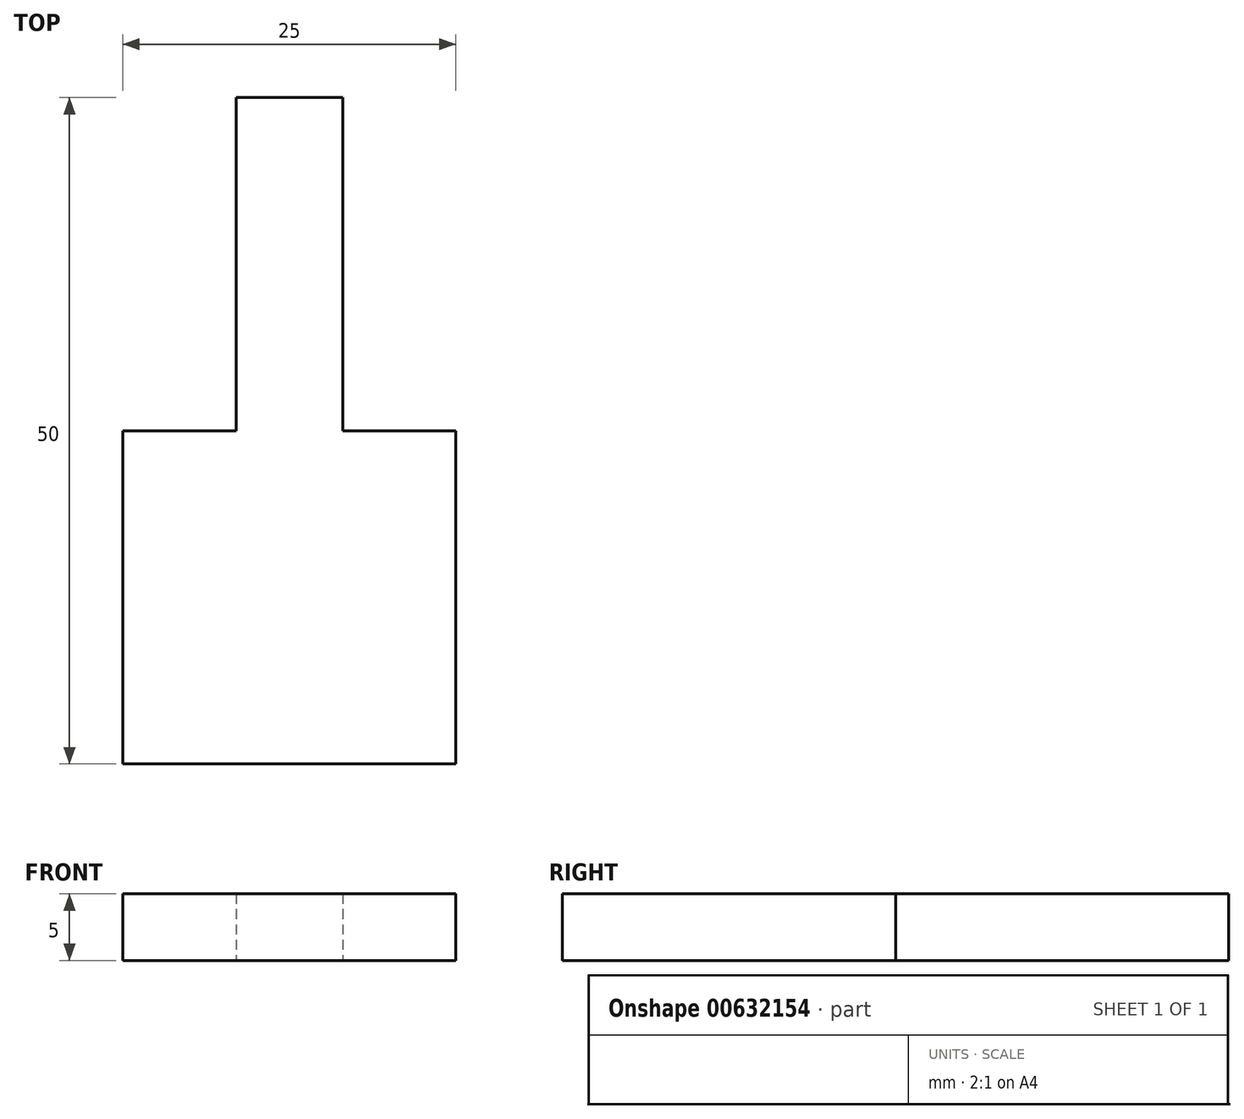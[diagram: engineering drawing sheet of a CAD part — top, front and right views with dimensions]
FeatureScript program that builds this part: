
annotation { "Feature Type Name" : "Feature", "Feature Type Description" : "" }
export const myFeature = defineFeature(function(context is Context, id is Id, definition is map)
    precondition{}
    {
        {
            var Q0;
            Q0=qCreatedBy(makeId("Top.planeOp"),FACE);
            var sketch = newSketch(context, id + "F0", { "sketchPlane" : qUnion([Q0])});
            skLineSegment(sketch, "E0.bottom", {"start": v(4, -12.5) * mm, "end": v(-4, -12.5) * mm});
            skLineSegment(sketch, "E0.top", {"start": v(4, 12.5) * mm, "end": v(-4, 12.5) * mm});
            skLineSegment(sketch, "E0.left", {"start": v(4, -12.5) * mm, "end": v(4, 12.5) * mm});
            skLineSegment(sketch, "E0.right", {"start": v(-4, -12.5) * mm, "end": v(-4, 12.5) * mm});
            skPoint(sketch, "E0.middle", {"position": v(0, 0) * mm});
            skLineSegment(sketch, "E1.bottom", {"start": v(-12.5, -12.5) * mm, "end": v(12.5, -12.5) * mm});
            skLineSegment(sketch, "E1.top", {"start": v(-12.5, -37.5) * mm, "end": v(12.5, -37.5) * mm});
            skLineSegment(sketch, "E1.left", {"start": v(-12.5, -12.5) * mm, "end": v(-12.5, -37.5) * mm});
            skLineSegment(sketch, "E1.right", {"start": v(12.5, -12.5) * mm, "end": v(12.5, -37.5) * mm});
            skLineSegment(sketch, "E2.bottom", {"start": v(0.25, -12.5) * mm, "end": v(-0.25, -12.5) * mm});
            skLineSegment(sketch, "E2.top", {"start": v(0.25, 12.5) * mm, "end": v(-0.25, 12.5) * mm});
            skLineSegment(sketch, "E2.left", {"start": v(0.25, -12.5) * mm, "end": v(0.25, 12.5) * mm});
            skLineSegment(sketch, "E2.right", {"start": v(-0.25, -12.5) * mm, "end": v(-0.25, 12.5) * mm});
            skSolve(sketch);
        }
        {
            var Q0;
            Q0 = qSketchRegion(id + "F0", true);
            extrude(context, id + "F1", {"entities" : qUnion([Q0]), "depth" : 5 * mm, "offsetDistance" : 25 * mm});
        }
    });
